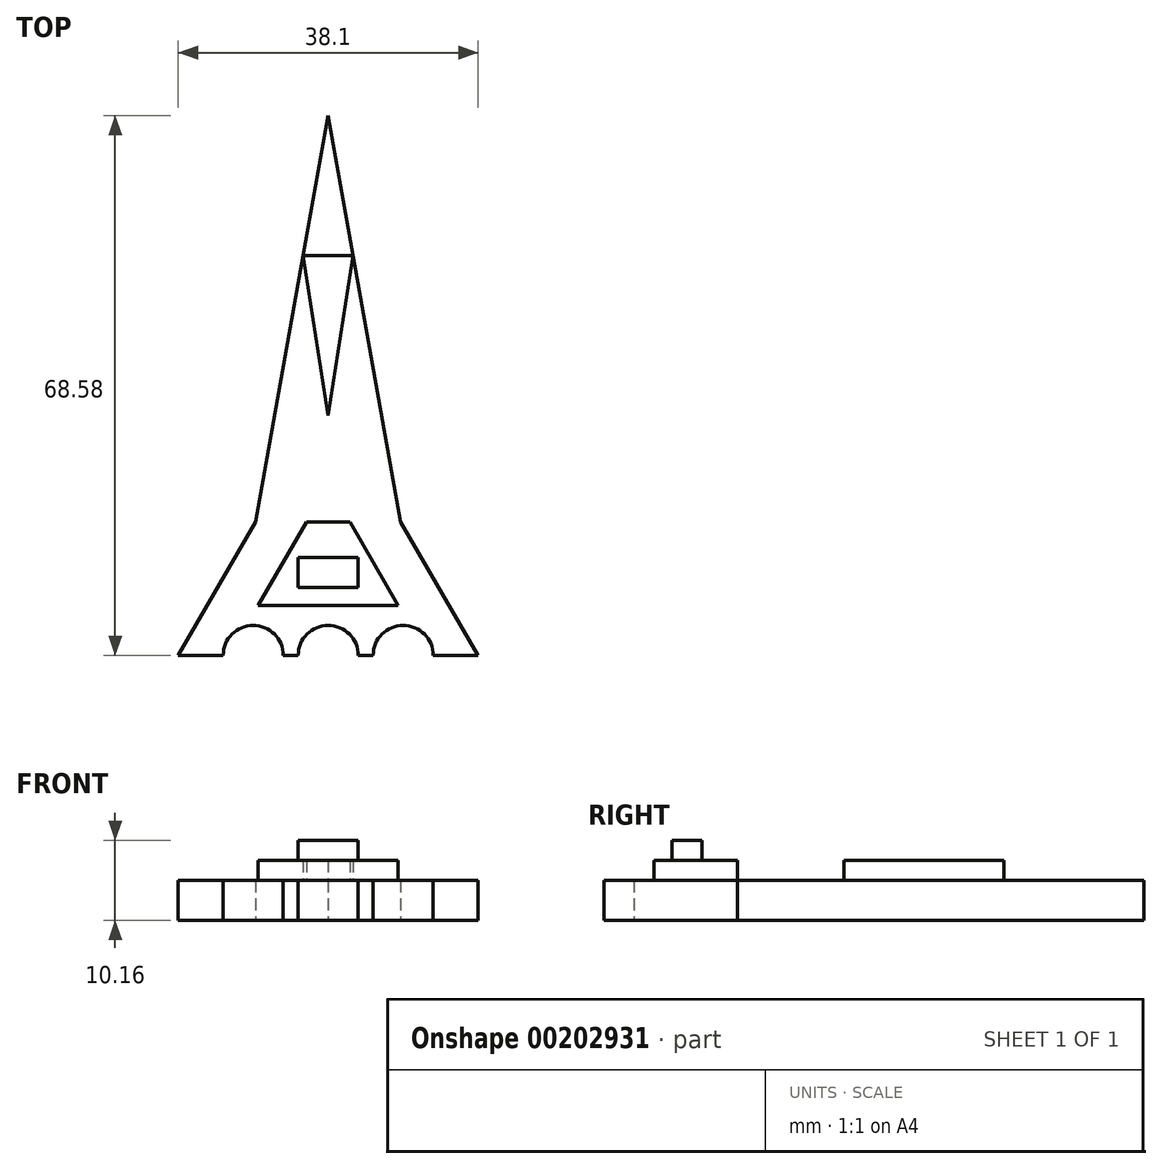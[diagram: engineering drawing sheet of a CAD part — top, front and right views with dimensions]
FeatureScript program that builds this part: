
annotation { "Feature Type Name" : "Feature", "Feature Type Description" : "" }
export const myFeature = defineFeature(function(context is Context, id is Id, definition is map)
    precondition{}
    {
        {
            var Q0;
            Q0=qCreatedBy(makeId("Top.planeOp"),FACE);
            var sketch = newSketch(context, id + "F0", { "sketchPlane" : qUnion([Q0])});
            skLineSegment(sketch, "E0.bottom", {"start": v(0, 0) * mm, "end": v(38.1, 0) * mm});
            skLineSegment(sketch, "E0.top", {"start": v(0, 50.8) * mm, "end": v(38.1, 50.8) * mm});
            skLineSegment(sketch, "E0.left", {"start": v(0, 0) * mm, "end": v(0, 50.8) * mm});
            skLineSegment(sketch, "E0.right", {"start": v(38.1, 0) * mm, "end": v(38.1, 50.8) * mm});
            skLineSegment(sketch, "E1", {"start": v(38.1, 0) * mm, "end": v(28.27, 16.93) * mm});
            skLineSegment(sketch, "E2", {"start": v(28.27, 16.93) * mm, "end": v(22.22, 50.8) * mm});
            skLineSegment(sketch, "E3", {"start": v(0, 16.93) * mm, "end": v(38.1, 16.93) * mm});
            skLineSegment(sketch, "E4", {"start": v(19.05, 50.8) * mm, "end": v(19.05, 0) * mm});
            skLineSegment(sketch, "E5.MirrorCS", {"start": v(9.83, 16.93) * mm, "end": v(15.88, 50.8) * mm});
            skLineSegment(sketch, "E6.MirrorCS", {"start": v(0, 0) * mm, "end": v(9.83, 16.93) * mm});
            skLineSegment(sketch, "E7", {"start": v(10.16, 6.35) * mm, "end": v(16.3, 16.93) * mm});
            skLineSegment(sketch, "E8", {"start": v(16.3, 16.93) * mm, "end": v(21.8, 16.93) * mm});
            skLineSegment(sketch, "E9", {"start": v(27.94, 6.35) * mm, "end": v(21.8, 16.93) * mm});
            skLineSegment(sketch, "E10", {"start": v(10.16, 6.35) * mm, "end": v(27.94, 6.35) * mm});
            skPoint(sketch, "E11", {"position": v(19.05, 6.35) * mm});
            skLineSegment(sketch, "E12", {"start": v(22.22, 50.8) * mm, "end": v(19.05, 30.48) * mm});
            skLineSegment(sketch, "E13", {"start": v(19.05, 30.48) * mm, "end": v(15.88, 50.8) * mm});
            skLineSegment(sketch, "E14.bottom", {"start": v(15.24, 12.45) * mm, "end": v(22.86, 12.45) * mm});
            skLineSegment(sketch, "E14.top", {"start": v(15.24, 8.64) * mm, "end": v(22.86, 8.64) * mm});
            skLineSegment(sketch, "E14.left", {"start": v(15.24, 12.45) * mm, "end": v(15.24, 8.64) * mm});
            skLineSegment(sketch, "E14.right", {"start": v(22.86, 12.45) * mm, "end": v(22.86, 8.64) * mm});
            skPoint(sketch, "E15", {"position": v(19.05, 12.45) * mm});
            skPoint(sketch, "E16", {"position": v(9.52, 0) * mm});
            skPoint(sketch, "E17", {"position": v(28.57, 0) * mm});
            skLineSegment(sketch, "E18", {"start": v(0, 0) * mm, "end": v(19.05, 0) * mm});
            skLineSegment(sketch, "E19", {"start": v(19.05, 0) * mm, "end": v(0, 0) * mm});
            skLineSegment(sketch, "E20", {"start": v(22.22, 50.8) * mm, "end": v(19.05, 68.58) * mm});
            skLineSegment(sketch, "E21", {"start": v(19.05, 68.58) * mm, "end": v(15.88, 50.8) * mm});
            skSolve(sketch);
        }
        {
            var Q0;
            {var subQ6=sQuery(id+"F0.wireOp",EDGE,"E6.MirrorCS");Q0=makeQuery(id+"F0.imprint","IMPRINT",FACE,{"disambiguationData":[TD([[makeQuery(id+"F0.imprint","IMPRINT",EDGE,{"derivedFrom":subQ6}),-1.0]])]});}
            var Q1;
            {var subQ5=sQuery(id+"F0.wireOp",EDGE,"E1");Q1=makeQuery(id+"F0.imprint","IMPRINT",FACE,{"disambiguationData":[TD([[makeQuery(id+"F0.imprint","IMPRINT",EDGE,{"derivedFrom":subQ5}),1.0]])]});}
            var Q2;
            {var subQ5=sQuery(id+"F0.wireOp",EDGE,"E2");Q2=makeQuery(id+"F0.imprint","IMPRINT",FACE,{"disambiguationData":[TD([[makeQuery(id+"F0.imprint","IMPRINT",EDGE,{"derivedFrom":subQ5}),1.0]])]});}
            var Q3;
            {var subQ5=sQuery(id+"F0.wireOp",EDGE,"E5.MirrorCS");Q3=makeQuery(id+"F0.imprint","IMPRINT",FACE,{"disambiguationData":[TD([[makeQuery(id+"F0.imprint","IMPRINT",EDGE,{"derivedFrom":subQ5}),-1.0]])]});}
            var Q4;
            {var subQ3=sQuery(id+"F0.wireOp",EDGE,"E20");Q4=makeQuery(id+"F0.imprint","IMPRINT",FACE,{"disambiguationData":[TD([[makeQuery(id+"F0.imprint","IMPRINT",EDGE,{"derivedFrom":subQ3}),1.0]])]});}
            var Q5;
            {var subQ0=sQuery(id+"F0.wireOp",EDGE,"E12");Q5=makeQuery(id+"F0.imprint","IMPRINT",FACE,{"disambiguationData":[TD([[makeQuery(id+"F0.imprint","IMPRINT",EDGE,{"derivedFrom":subQ0}),-1.0]])]});}
            var Q6;
            {var subQ3=sQuery(id+"F0.wireOp",EDGE,"E13");Q6=makeQuery(id+"F0.imprint","IMPRINT",FACE,{"disambiguationData":[TD([[makeQuery(id+"F0.imprint","IMPRINT",EDGE,{"derivedFrom":subQ3}),-1.0]])]});}
            extrude(context, id + "F1", {"entities" : qUnion([Q0, Q1, Q2, Q3, Q4, Q5, Q6]), "depth" : 5.08 * mm});
        }
        {
            var Q0;
            {var subQ1=sQuery(id+"F0.wireOp",EDGE,"E7");Q0=makeQuery(id+"F0.imprint","IMPRINT",FACE,{"disambiguationData":[TD([[makeQuery(id+"F0.imprint","IMPRINT",EDGE,{"derivedFrom":subQ1}),-1.0]])]});}
            var Q1;
            {var subQ0=sQuery(id+"F0.wireOp",EDGE,"E9");Q1=makeQuery(id+"F0.imprint","IMPRINT",FACE,{"disambiguationData":[TD([[makeQuery(id+"F0.imprint","IMPRINT",EDGE,{"derivedFrom":subQ0}),1.0]])]});}
            extrude(context, id + "F2", {"entities" : qUnion([Q0, Q1]), "operationType" : NewBodyOperationType.ADD, "depth" : 7.62 * mm});
        }
        {
            var Q0;
            {var subQ5=sQuery(id+"F0.wireOp",EDGE,"E14.left");Q0=makeQuery(id+"F0.imprint","IMPRINT",FACE,{"disambiguationData":[TD([[makeQuery(id+"F0.imprint","IMPRINT",EDGE,{"derivedFrom":subQ5}),1.0]])]});}
            var Q1;
            {var subQ5=sQuery(id+"F0.wireOp",EDGE,"E14.right");Q1=makeQuery(id+"F0.imprint","IMPRINT",FACE,{"disambiguationData":[TD([[makeQuery(id+"F0.imprint","IMPRINT",EDGE,{"derivedFrom":subQ5}),-1.0]])]});}
            extrude(context, id + "F3", {"entities" : qUnion([Q0, Q1]), "operationType" : NewBodyOperationType.ADD, "depth" : 10.16 * mm});
        }
        {
            var Q0;
            {var subQ3=sQuery(id+"F0.wireOp",EDGE,"E13");Q0=makeQuery(id+"F0.imprint","IMPRINT",FACE,{"disambiguationData":[TD([[makeQuery(id+"F0.imprint","IMPRINT",EDGE,{"derivedFrom":subQ3}),-1.0]])]});}
            var Q1;
            {var subQ0=sQuery(id+"F0.wireOp",EDGE,"E12");Q1=makeQuery(id+"F0.imprint","IMPRINT",FACE,{"disambiguationData":[TD([[makeQuery(id+"F0.imprint","IMPRINT",EDGE,{"derivedFrom":subQ0}),-1.0]])]});}
            extrude(context, id + "F4", {"entities" : qUnion([Q0, Q1]), "operationType" : NewBodyOperationType.ADD, "depth" : 7.62 * mm});
        }
        {
            var Q0;
            Q0=sQuery(id+"F0.wireOp",VERTEX,"E4.end");
            var Q1;
            Q1=makeQuery(id+"F1.opExtrude","SWEPT_BODY",BODY,{"disambiguationData":[OSD([sQuery(id+"F0.wireOp",EDGE,"E0.bottom"),sQuery(id+"F0.wireOp",EDGE,"E1"),sQuery(id+"F0.wireOp",EDGE,"E2"),sQuery(id+"F0.wireOp",EDGE,"E5.MirrorCS"),sQuery(id+"F0.wireOp",EDGE,"E6.MirrorCS"),sQuery(id+"F0.wireOp",EDGE,"E7"),sQuery(id+"F0.wireOp",EDGE,"E8"),sQuery(id+"F0.wireOp",EDGE,"E9"),sQuery(id+"F0.wireOp",EDGE,"E10"),sQuery(id+"F0.wireOp",EDGE,"E12"),sQuery(id+"F0.wireOp",EDGE,"E13")])]});
            hole(context, id + "F5", {"style" : HoleStyle.SIMPLE, "endStyle" : HoleEndStyle.THROUGH, "oppositeDirection" : true, "holeDiameter" : 7.62 * mm, "locations" : qUnion([Q0]), "scope" : qUnion([Q1]), "isTappedThrough" : true});
        }
        {
            var Q0;
            Q0=sQuery(id+"F0.wireOp",VERTEX,"E16");
            var Q1;
            Q1=sQuery(id+"F0.wireOp",VERTEX,"E17");
            var Q2;
            Q2=makeQuery(id+"F1.opExtrude","SWEPT_BODY",BODY,{"disambiguationData":[OSD([sQuery(id+"F0.wireOp",EDGE,"E0.bottom"),sQuery(id+"F0.wireOp",EDGE,"E1"),sQuery(id+"F0.wireOp",EDGE,"E2"),sQuery(id+"F0.wireOp",EDGE,"E5.MirrorCS"),sQuery(id+"F0.wireOp",EDGE,"E6.MirrorCS"),sQuery(id+"F0.wireOp",EDGE,"E7"),sQuery(id+"F0.wireOp",EDGE,"E8"),sQuery(id+"F0.wireOp",EDGE,"E9"),sQuery(id+"F0.wireOp",EDGE,"E10"),sQuery(id+"F0.wireOp",EDGE,"E12"),sQuery(id+"F0.wireOp",EDGE,"E13"),sQuery(id+"F0.wireOp",EDGE,"E19")])]});
            hole(context, id + "F6", {"style" : HoleStyle.SIMPLE, "endStyle" : HoleEndStyle.THROUGH, "oppositeDirection" : true, "holeDiameter" : 7.62 * mm, "locations" : qUnion([Q0, Q1]), "scope" : qUnion([Q2]), "isTappedThrough" : true});
        }
    });
